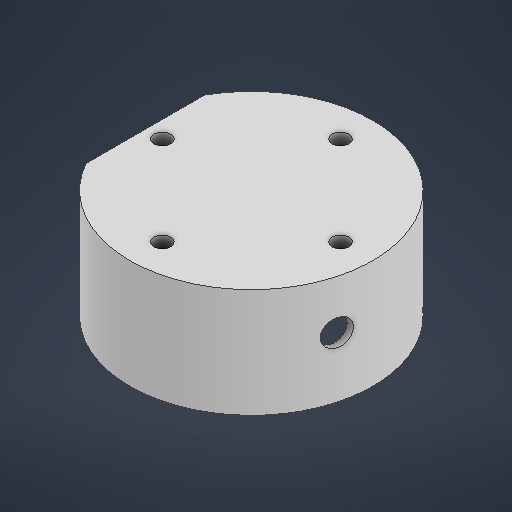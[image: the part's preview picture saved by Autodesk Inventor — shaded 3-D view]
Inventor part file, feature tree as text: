
AUTODESK INVENTOR PART (.ipt)
format: ipt  version: 2025 (Build 290162000, 162)  size: 249,856 bytes
history: native  units: in
note: dims shown in document units (in); Inventor stores cm internally (conversion verified against a paired STEP export)
features: sketch x6, extrude x5
ambient origin geometry x8: Origin, YZ Plane, XZ Plane, XY Plane, X Axis, Y Axis, Z Axis, Center Point
bodies: Solid1 (feature_tree)
feature tree (11):
  extrude  "Extrusion1"  Depth=0.7874in
  extrude  "Extrusion3"  Depth=0.2165in
  extrude  "Extrusion4"  Depth=0.3937in TaperAngle=0.0deg
  extrude  "Extrusion5"  TaperAngle=0.0deg  [1 undecoded]
  extrude  "Extrusion6"  Depth=0.1181in TaperAngle=0.0deg
  sketch  "Sketch1"  dims[d0=3.1102in d1=0.7874in]
  sketch  "Sketch Circular Pattern1"  dims[d2=2.2835in d3=0.2165in]
  sketch  "Sketch3"  dims[d4=1.5748in d6=360.0deg d8=0.3937in d9=0.0in]
  sketch  "Sketch4"  dims[d18=0.1969in d19=0.0in d20=0.0in]
  sketch  "Sketch5"  dims[d21=0.8in d22=0.1181in d23=0.0in]
  sketch  "Sketch6"  dims[d24=0.0787in d25=0.0591in d26=0.0787in d27=0.0787in d28=1.0in d29=0.0in d30=0.0167in d31=0.0in d32=0.2953in]
note: 1 required parameter value undecoded (feature->parameter linkage not recoverable at this tier; creation-order binding heuristic only, values carry confidence <= 0.55)
